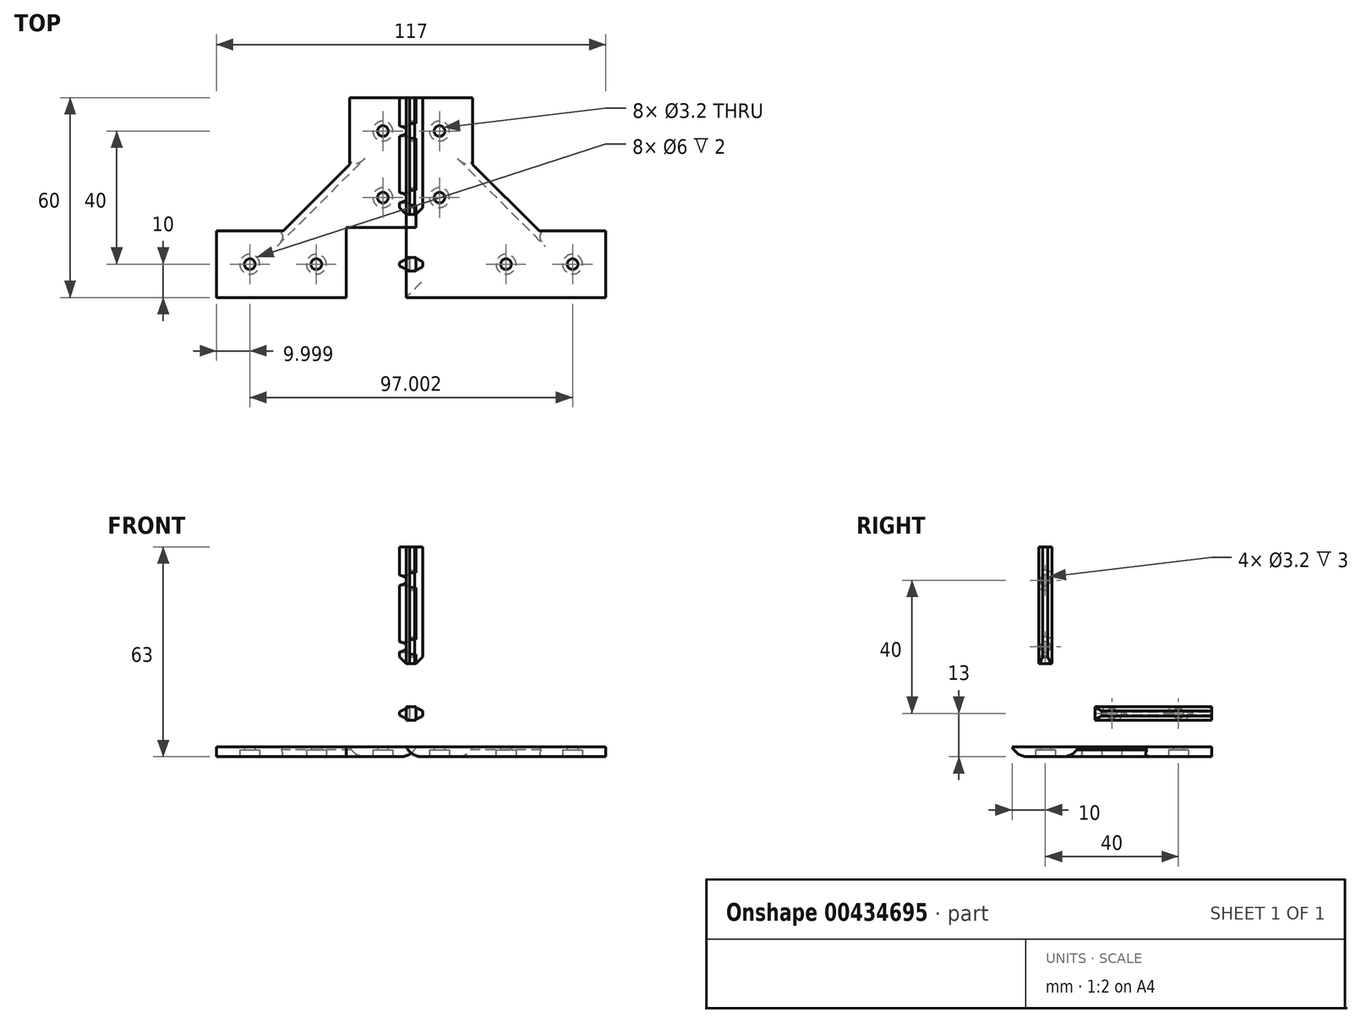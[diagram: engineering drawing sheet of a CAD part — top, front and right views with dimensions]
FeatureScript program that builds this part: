
annotation { "Feature Type Name" : "Feature", "Feature Type Description" : "" }
export const myFeature = defineFeature(function(context is Context, id is Id, definition is map)
    precondition{}
    {
        {
            var Q0;
            Q0=qCreatedBy(makeId("Right.planeOp"),FACE);
            var sketch = newSketch(context, id + "F0", { "sketchPlane" : qUnion([Q0])});
            skLineSegment(sketch, "E0", {"start": v(0, 0) * mm, "end": v(0, 50) * mm, "construction": true});
            skLineSegment(sketch, "E1", {"start": v(0, 0) * mm, "end": v(50, 0) * mm, "construction": true});
            skLineSegment(sketch, "E2", {"start": v(50, 10) * mm, "end": v(50, -10) * mm, "construction": true});
            skLineSegment(sketch, "E3", {"start": v(-10, 50) * mm, "end": v(10, 50) * mm, "construction": true});
            skLineSegment(sketch, "E4", {"start": v(-10, 50) * mm, "end": v(-10, -10) * mm});
            skLineSegment(sketch, "E5", {"start": v(50, -10) * mm, "end": v(-10, -10) * mm});
            skLineSegment(sketch, "E6.MirrorCS", {"start": v(10, 50) * mm, "end": v(10, 10) * mm, "construction": true});
            skLineSegment(sketch, "E7.MirrorCS", {"start": v(50, 10) * mm, "end": v(10, 10) * mm, "construction": true});
            skLineSegment(sketch, "E8", {"start": v(-10, 50) * mm, "end": v(10, 50) * mm});
            skLineSegment(sketch, "E9", {"start": v(50, 10) * mm, "end": v(50, -10) * mm});
            skLineSegment(sketch, "E10", {"start": v(50, 10) * mm, "end": v(10, 50) * mm, "construction": true});
            skLineSegment(sketch, "E11", {"start": v(10, 10) * mm, "end": v(10, -10) * mm, "construction": true});
            skLineSegment(sketch, "E12", {"start": v(10, 10) * mm, "end": v(-10, 10) * mm, "construction": true});
            skCircle(sketch, "E13", {"center": v(0, 40) * mm, "radius": 2 * mm, "construction": true});
            skCircle(sketch, "E14", {"center": v(0, 20) * mm, "radius": 2 * mm, "construction": true});
            skCircle(sketch, "E15", {"center": v(20, 0) * mm, "radius": 2 * mm, "construction": true});
            skCircle(sketch, "E16", {"center": v(40, 0) * mm, "radius": 2 * mm, "construction": true});
            skPoint(sketch, "E17", {"position": v(-2, 40) * mm});
            skPoint(sketch, "E18", {"position": v(2, 40) * mm});
            skPoint(sketch, "E19", {"position": v(-2, 20) * mm});
            skPoint(sketch, "E20", {"position": v(2, 20) * mm});
            skLineSegment(sketch, "E21", {"start": v(-2, 50) * mm, "end": v(-2, 15) * mm});
            skLineSegment(sketch, "E22", {"start": v(-2, 15) * mm, "end": v(2, 15) * mm});
            skLineSegment(sketch, "E23", {"start": v(2, 15) * mm, "end": v(2, 50) * mm});
            skPoint(sketch, "E24", {"position": v(20, -2) * mm});
            skPoint(sketch, "E25", {"position": v(20, 2) * mm});
            skPoint(sketch, "E26", {"position": v(40, 2) * mm});
            skPoint(sketch, "E27", {"position": v(40, -2) * mm});
            skLineSegment(sketch, "E28", {"start": v(15, 2) * mm, "end": v(15, -2) * mm});
            skLineSegment(sketch, "E29", {"start": v(50, 2) * mm, "end": v(15, 2) * mm});
            skLineSegment(sketch, "E30", {"start": v(50, -2) * mm, "end": v(15, -2) * mm});
            skLineSegment(sketch, "E31", {"start": v(10, 30) * mm, "end": v(30, 10) * mm});
            skLineSegment(sketch, "E32", {"start": v(30, 10) * mm, "end": v(50, 10) * mm});
            skLineSegment(sketch, "E33", {"start": v(10, 30) * mm, "end": v(10, 50) * mm});
            skLineSegment(sketch, "E34", {"start": v(11, 10) * mm, "end": v(11, -10) * mm});
            skLineSegment(sketch, "E35", {"start": v(10, 11) * mm, "end": v(-10, 11) * mm});
            skLineSegment(sketch, "E36", {"start": v(11, 10) * mm, "end": v(10, 10) * mm, "construction": true});
            skLineSegment(sketch, "E37", {"start": v(10, 11) * mm, "end": v(10, 10) * mm, "construction": true});
            skLineSegment(sketch, "E38", {"start": v(11, 10) * mm, "end": v(11, 11) * mm});
            skLineSegment(sketch, "E39", {"start": v(11, 11) * mm, "end": v(10, 11) * mm});
            skSolve(sketch);
        }
        {
            var Q0;
            {var subQ7=sQuery(id+"F0.wireOp",EDGE,"E4");Q0=makeQuery(id+"F0.imprint","IMPRINT",FACE,{"disambiguationData":[TD([[makeQuery(id+"F0.imprint","IMPRINT",EDGE,{"derivedFrom":subQ7}),1.0]])]});}
            var Q1;
            {var subQ0=sQuery(id+"F0.wireOp",EDGE,"E21");Q1=makeQuery(id+"F0.imprint","IMPRINT",FACE,{"disambiguationData":[TD([[makeQuery(id+"F0.imprint","IMPRINT",EDGE,{"derivedFrom":subQ0}),1.0]])]});}
            var Q2;
            Q2=makeQuery(id+"F0.imprint","IMPRINT",FACE,{"disambiguationData":[TD([[makeQuery(id+"F0.imprint","IMPRINT",EDGE,{"derivedFrom":sQuery(id+"F0.wireOp",EDGE,"E28")}),1.0]])]});
            var Q3;
            {var subQ1=sQuery(id+"F0.wireOp",EDGE,"E21");Q3=makeQuery(id+"F0.imprint","IMPRINT",FACE,{"disambiguationData":[TD([[makeQuery(id+"F0.imprint","IMPRINT",EDGE,{"derivedFrom":subQ1}),-1.0]])]});}
            extrude(context, id + "F1", {"entities" : qUnion([Q0, Q1, Q2, Q3]), "depth" : 3 * mm});
        }
        {
            var Q0;
            Q0=makeQuery(id+"F1.opExtrude","CAP_FACE",FACE,{"disambiguationData":[OSD([sQuery(id+"F0.wireOp",EDGE,"E4"),sQuery(id+"F0.wireOp",EDGE,"E5"),sQuery(id+"F0.wireOp",EDGE,"E8"),sQuery(id+"F0.wireOp",EDGE,"E9"),sQuery(id+"F0.wireOp",EDGE,"E10")])],"isStart":false});
            var sketch = newSketch(context, id + "F2", { "sketchPlane" : qUnion([Q0])});
            skPoint(sketch, "E40.0", {"position": v(0, 40) * mm});
            skPoint(sketch, "E40.1", {"position": v(0, 20) * mm});
            skPoint(sketch, "E40.2", {"position": v(20, 0) * mm});
            skPoint(sketch, "E40.3", {"position": v(40, 0) * mm});
            skSolve(sketch);
        }
        {
            var Q0;
            Q0=makeQuery(id+"F1.opExtrude","CAP_FACE",FACE,{"disambiguationData":[OSD([sQuery(id+"F0.wireOp",EDGE,"E4"),sQuery(id+"F0.wireOp",EDGE,"E5"),sQuery(id+"F0.wireOp",EDGE,"E8"),sQuery(id+"F0.wireOp",EDGE,"E9"),sQuery(id+"F0.wireOp",EDGE,"E10")])],"isStart":false});
            var sketch = newSketch(context, id + "F3", { "sketchPlane" : qUnion([Q0])});
            skLineSegment(sketch, "E41.0", {"start": v(50, 2) * mm, "end": v(15, 2) * mm});
            skLineSegment(sketch, "E41.1", {"start": v(50, -2) * mm, "end": v(15, -2) * mm});
            skLineSegment(sketch, "E41.2", {"start": v(15, 2) * mm, "end": v(15, -2) * mm});
            skLineSegment(sketch, "E41.3", {"start": v(50, 10) * mm, "end": v(50, -10) * mm});
            skLineSegment(sketch, "E41.4", {"start": v(-2, 15) * mm, "end": v(2, 15) * mm});
            skLineSegment(sketch, "E41.5", {"start": v(-2, 50) * mm, "end": v(-2, 15) * mm});
            skLineSegment(sketch, "E41.6", {"start": v(2, 15) * mm, "end": v(2, 50) * mm});
            skLineSegment(sketch, "E41.7", {"start": v(-10, 50) * mm, "end": v(10, 50) * mm});
            skSolve(sketch);
        }
        {
            var Q0;
            Q0=qSketchRegion(id+"F3",true);
            extrude(context, id + "F4", {"entities" : qUnion([Q0]), "oppositeDirection" : true, "depth" : 5 * mm});
        }
        {
            var Q0;
            Q0=makeQuery(id+"F4.opExtrude","CAP_EDGE",EDGE,{"disambiguationData":[OSD([sQuery(id+"F3.wireOp",EDGE,"E41.0")])],"isStart":false});
            var Q1;
            Q1=makeQuery(id+"F4.opExtrude","CAP_EDGE",EDGE,{"disambiguationData":[OSD([sQuery(id+"F3.wireOp",EDGE,"E41.1")])],"isStart":false});
            var Q2;
            Q2=makeQuery(id+"F4.opExtrude","CAP_EDGE",EDGE,{"disambiguationData":[OSD([sQuery(id+"F3.wireOp",EDGE,"E41.6")])],"isStart":false});
            var Q3;
            Q3=makeQuery(id+"F4.opExtrude","CAP_EDGE",EDGE,{"disambiguationData":[OSD([sQuery(id+"F3.wireOp",EDGE,"E41.5")])],"isStart":false});
            chamfer(context, id + "F5", {"entities" : qUnion([Q0, Q1, Q2, Q3]), "chamferType" : ChamferType.TWO_OFFSETS, "width1" : 3 * mm, "oppositeDirection" : false, "width2" : 1.5 * mm, "tangentPropagation" : true});
        }
        {
            var Q0;
            Q0=sQuery(id+"F2.wireOp",VERTEX,"E40.0");
            var Q1;
            Q1=sQuery(id+"F2.wireOp",VERTEX,"E40.1");
            var Q2;
            Q2=sQuery(id+"F2.wireOp",VERTEX,"E40.2");
            var Q3;
            Q3=sQuery(id+"F2.wireOp",VERTEX,"E40.3");
            var Q4;
            Q4=makeQuery(id+"F1.opExtrude","SWEPT_BODY",BODY,{"disambiguationData":[OSD([sQuery(id+"F0.wireOp",EDGE,"E4"),sQuery(id+"F0.wireOp",EDGE,"E5"),sQuery(id+"F0.wireOp",EDGE,"E8"),sQuery(id+"F0.wireOp",EDGE,"E9"),sQuery(id+"F0.wireOp",EDGE,"E10")])]});
            var Q5;
            Q5=makeQuery(id+"F4.opExtrude","SWEPT_BODY",BODY,{"disambiguationData":[OSD([sQuery(id+"F3.wireOp",EDGE,"E41.0"),sQuery(id+"F3.wireOp",EDGE,"E41.1"),sQuery(id+"F3.wireOp",EDGE,"E41.2"),sQuery(id+"F3.wireOp",EDGE,"E41.3")])]});
            var Q6;
            Q6=makeQuery(id+"F4.opExtrude","SWEPT_BODY",BODY,{"disambiguationData":[OSD([sQuery(id+"F3.wireOp",EDGE,"E41.4"),sQuery(id+"F3.wireOp",EDGE,"E41.5"),sQuery(id+"F3.wireOp",EDGE,"E41.6"),sQuery(id+"F3.wireOp",EDGE,"E41.7")])]});
            hole(context, id + "F6", {"style" : HoleStyle.C_BORE, "endStyle" : HoleEndStyle.THROUGH, "holeDiameter" : 3.2 * mm, "cBoreDiameter" : 6 * mm, "cBoreDepth" : 2 * mm, "isTappedThrough" : true, "tappedDepth" : 12 * mm, "tapClearance" : 3, "startFromSketch" : true, "locations" : qUnion([Q0, Q1, Q2, Q3]), "scope" : qUnion([Q4, Q5, Q6])});
        }
        {
            var Q0;
            Q0=makeQuery(id+"F1.opExtrude","CAP_EDGE",EDGE,{"disambiguationData":[OSD([sQuery(id+"F0.wireOp",EDGE,"E4")])],"isStart":false});
            var Q1;
            Q1=makeQuery(id+"F1.opExtrude","CAP_EDGE",EDGE,{"disambiguationData":[OSD([sQuery(id+"F0.wireOp",EDGE,"E5")])],"isStart":false});
            var Q2;
            Q2=makeQuery(id+"F1.opExtrude","CAP_EDGE",EDGE,{"disambiguationData":[OSD([sQuery(id+"F0.wireOp",EDGE,"E33")])],"isStart":false});
            var Q3;
            Q3=makeQuery(id+"F1.opExtrude","CAP_EDGE",EDGE,{"disambiguationData":[OSD([sQuery(id+"F0.wireOp",EDGE,"E32")])],"isStart":false});
            fillet(context, id + "F7", {"entities" : qUnion([Q0, Q1, Q2, Q3]), "radius" : 5 * mm, "tangentPropagation" : true, "allowEdgeOverflow" : false});
        }
        {
            var Q0;
            Q0=makeQuery(id+"F1.opExtrude","CAP_EDGE",EDGE,{"disambiguationData":[OSD([sQuery(id+"F0.wireOp",EDGE,"E31")])],"isStart":false});
            chamfer(context, id + "F8", {"entities" : qUnion([Q0]), "width" : 2 * mm, "tangentPropagation" : true});
        }
        {
            var Q0;
            Q0=makeQuery(id+"F4.opExtrude","CAP_EDGE",EDGE,{"disambiguationData":[OSD([sQuery(id+"F3.wireOp",EDGE,"E41.2")])],"isStart":false});
            var Q1;
            Q1=makeQuery(id+"F4.opExtrude","CAP_EDGE",EDGE,{"disambiguationData":[OSD([sQuery(id+"F3.wireOp",EDGE,"E41.4")])],"isStart":false});
            chamfer(context, id + "F9", {"entities" : qUnion([Q0, Q1]), "width" : 2 * mm, "tangentPropagation" : true});
        }
        {
            var Q0;
            Q0=makeQuery(id+"F1.opExtrude","SWEPT_BODY",BODY,{"disambiguationData":[OSD([sQuery(id+"F0.wireOp",EDGE,"E4"),sQuery(id+"F0.wireOp",EDGE,"E5"),sQuery(id+"F0.wireOp",EDGE,"E8"),sQuery(id+"F0.wireOp",EDGE,"E9"),sQuery(id+"F0.wireOp",EDGE,"E31"),sQuery(id+"F0.wireOp",EDGE,"E32"),sQuery(id+"F0.wireOp",EDGE,"E33")])]});
            var Q1;
            Q1=sQuery(id+"F0.wireOp",EDGE,"E5");
            transform(context, id + "F10", {"entities" : qUnion([Q0]), "transformType" : TransformType.ROTATION, "transformAxis" : qUnion([Q1]), "angle" : 270 * degree, "makeCopy" : false});
        }
        {
            var Q0;
            {var subQ0=sQuery(id+"F0.wireOp",EDGE,"E21");Q0=makeQuery(id+"F0.imprint","IMPRINT",FACE,{"disambiguationData":[TD([[makeQuery(id+"F0.imprint","IMPRINT",EDGE,{"derivedFrom":subQ0}),1.0]])]});}
            var Q1;
            Q1=makeQuery(id+"F0.imprint","IMPRINT",FACE,{"disambiguationData":[TD([[makeQuery(id+"F0.imprint","IMPRINT",EDGE,{"derivedFrom":sQuery(id+"F0.wireOp",EDGE,"E28")}),1.0]])]});
            var Q2;
            {var subQ1=sQuery(id+"F0.wireOp",EDGE,"E21");Q2=makeQuery(id+"F0.imprint","IMPRINT",FACE,{"disambiguationData":[TD([[makeQuery(id+"F0.imprint","IMPRINT",EDGE,{"derivedFrom":subQ1}),-1.0]])]});}
            extrude(context, id + "F11", {"entities" : qUnion([Q0, Q1, Q2]), "depth" : 3 * mm});
        }
        {
            var Q0;
            Q0=makeQuery(id+"F0.imprint","IMPRINT",FACE,{"disambiguationData":[TD([[makeQuery(id+"F0.imprint","IMPRINT",EDGE,{"derivedFrom":sQuery(id+"F0.wireOp",EDGE,"E28")}),1.0]])]});
            var Q1;
            {var subQ0=sQuery(id+"F0.wireOp",EDGE,"E21");Q1=makeQuery(id+"F0.imprint","IMPRINT",FACE,{"disambiguationData":[TD([[makeQuery(id+"F0.imprint","IMPRINT",EDGE,{"derivedFrom":subQ0}),1.0]])]});}
            extrude(context, id + "F12", {"entities" : qUnion([Q0, Q1]), "depth" : 5 * mm});
        }
        {
            var Q0;
            Q0=makeQuery(id+"F12.opExtrude","CAP_EDGE",EDGE,{"disambiguationData":[OSD([sQuery(id+"F0.wireOp",EDGE,"E29")])],"isStart":false});
            var Q1;
            Q1=makeQuery(id+"F12.opExtrude","CAP_EDGE",EDGE,{"disambiguationData":[OSD([sQuery(id+"F0.wireOp",EDGE,"E30")])],"isStart":false});
            var Q2;
            Q2=makeQuery(id+"F12.opExtrude","CAP_EDGE",EDGE,{"disambiguationData":[OSD([sQuery(id+"F0.wireOp",EDGE,"E23")])],"isStart":false});
            var Q3;
            Q3=makeQuery(id+"F12.opExtrude","CAP_EDGE",EDGE,{"disambiguationData":[OSD([sQuery(id+"F0.wireOp",EDGE,"E21")])],"isStart":false});
            chamfer(context, id + "F13", {"entities" : qUnion([Q0, Q1, Q2, Q3]), "chamferType" : ChamferType.TWO_OFFSETS, "width1" : 1.25 * mm, "oppositeDirection" : false, "width2" : 2.5 * mm, "tangentPropagation" : true});
        }
        {
            var Q0;
            {var subQ1=sQuery(id+"F0.wireOp",EDGE,"E21");Q0=makeQuery(id+"F0.imprint","IMPRINT",FACE,{"disambiguationData":[TD([[makeQuery(id+"F0.imprint","IMPRINT",EDGE,{"derivedFrom":subQ1}),-1.0]])]});}
            var sketch = newSketch(context, id + "F14", { "sketchPlane" : qUnion([Q0])});
            skPoint(sketch, "E42.0", {"position": v(20, 0) * mm});
            skPoint(sketch, "E42.1", {"position": v(40, 0) * mm});
            skPoint(sketch, "E42.2", {"position": v(0, 20) * mm});
            skPoint(sketch, "E42.3", {"position": v(0, 40) * mm});
            skSolve(sketch);
        }
        {
            var Q0;
            Q0=sQuery(id+"F14.wireOp",VERTEX,"E42.3");
            var Q1;
            Q1=sQuery(id+"F14.wireOp",VERTEX,"E42.2");
            var Q2;
            Q2=sQuery(id+"F14.wireOp",VERTEX,"E42.0");
            var Q3;
            Q3=sQuery(id+"F14.wireOp",VERTEX,"E42.1");
            var Q4;
            Q4=makeQuery(id+"F11.opExtrude","SWEPT_BODY",BODY,{"disambiguationData":[OSD([sQuery(id+"F0.wireOp",EDGE,"E4"),sQuery(id+"F0.wireOp",EDGE,"E5"),sQuery(id+"F0.wireOp",EDGE,"E8"),sQuery(id+"F0.wireOp",EDGE,"E9"),sQuery(id+"F0.wireOp",EDGE,"E31"),sQuery(id+"F0.wireOp",EDGE,"E32"),sQuery(id+"F0.wireOp",EDGE,"E33"),sQuery(id+"F0.wireOp",EDGE,"E34"),sQuery(id+"F0.wireOp",EDGE,"E35"),sQuery(id+"F0.wireOp",EDGE,"E38"),sQuery(id+"F0.wireOp",EDGE,"E39")])]});
            hole(context, id + "F15", {"style" : HoleStyle.C_BORE, "endStyle" : HoleEndStyle.THROUGH, "oppositeDirection" : true, "holeDiameter" : 3.2 * mm, "cBoreDiameter" : 6 * mm, "cBoreDepth" : 2 * mm, "isTappedThrough" : true, "tappedDepth" : 12 * mm, "tapClearance" : 3, "startFromSketch" : true, "locations" : qUnion([Q0, Q1, Q2, Q3]), "scope" : qUnion([Q4])});
        }
        {
            var Q0;
            Q0=makeQuery(id+"F11.opExtrude","CAP_EDGE",EDGE,{"disambiguationData":[OSD([sQuery(id+"F0.wireOp",EDGE,"E4")])],"isStart":true});
            var Q1;
            Q1=makeQuery(id+"F11.opExtrude","CAP_EDGE",EDGE,{"disambiguationData":[OSD([sQuery(id+"F0.wireOp",EDGE,"E5")])],"isStart":true});
            var Q2;
            Q2=makeQuery(id+"F11.opExtrude","CAP_EDGE",EDGE,{"disambiguationData":[OSD([sQuery(id+"F0.wireOp",EDGE,"E33")])],"isStart":true});
            var Q3;
            Q3=makeQuery(id+"F11.opExtrude","CAP_EDGE",EDGE,{"disambiguationData":[OSD([sQuery(id+"F0.wireOp",EDGE,"E32")])],"isStart":true});
            fillet(context, id + "F16", {"entities" : qUnion([Q0, Q1, Q2, Q3]), "radius" : 5 * mm, "tangentPropagation" : true, "allowEdgeOverflow" : false});
        }
        {
            var Q0;
            Q0=makeQuery(id+"F11.opExtrude","CAP_EDGE",EDGE,{"disambiguationData":[OSD([sQuery(id+"F0.wireOp",EDGE,"E31")])],"isStart":true});
            chamfer(context, id + "F17", {"entities" : qUnion([Q0]), "width" : 2 * mm, "tangentPropagation" : true});
        }
        {
            var Q0;
            Q0=makeQuery(id+"F12.opExtrude","CAP_EDGE",EDGE,{"disambiguationData":[OSD([sQuery(id+"F0.wireOp",EDGE,"E28")])],"isStart":false});
            var Q1;
            Q1=makeQuery(id+"F12.opExtrude","CAP_EDGE",EDGE,{"disambiguationData":[OSD([sQuery(id+"F0.wireOp",EDGE,"E22")])],"isStart":false});
            chamfer(context, id + "F18", {"entities" : qUnion([Q0, Q1]), "width" : 2 * mm, "tangentPropagation" : true});
        }
        {
            var Q0;
            Q0=makeQuery(id+"F11.opExtrude","SWEPT_BODY",BODY,{"disambiguationData":[OSD([sQuery(id+"F0.wireOp",EDGE,"E4"),sQuery(id+"F0.wireOp",EDGE,"E5"),sQuery(id+"F0.wireOp",EDGE,"E8"),sQuery(id+"F0.wireOp",EDGE,"E9"),sQuery(id+"F0.wireOp",EDGE,"E31"),sQuery(id+"F0.wireOp",EDGE,"E32"),sQuery(id+"F0.wireOp",EDGE,"E33"),sQuery(id+"F0.wireOp",EDGE,"E34"),sQuery(id+"F0.wireOp",EDGE,"E35"),sQuery(id+"F0.wireOp",EDGE,"E38"),sQuery(id+"F0.wireOp",EDGE,"E39")])]});
            var Q1;
            {var subQ0=sQuery(id+"F0.wireOp",EDGE,"E5");Q1=makeQuery(id+"F16.opFillet","BLEND_EDGE",EDGE,{"blendedFrom":[makeQuery(id+"F11.opExtrude","CAP_EDGE",EDGE,{"disambiguationData":[OSD([subQ0])],"isStart":true}),makeQuery(id+"F11.opExtrude","CAP_FACE",FACE,{"disambiguationData":[OSD([sQuery(id+"F0.wireOp",EDGE,"E4"),subQ0,sQuery(id+"F0.wireOp",EDGE,"E8"),sQuery(id+"F0.wireOp",EDGE,"E9"),sQuery(id+"F0.wireOp",EDGE,"E31"),sQuery(id+"F0.wireOp",EDGE,"E32"),sQuery(id+"F0.wireOp",EDGE,"E33"),sQuery(id+"F0.wireOp",EDGE,"E34"),sQuery(id+"F0.wireOp",EDGE,"E35"),sQuery(id+"F0.wireOp",EDGE,"E38"),sQuery(id+"F0.wireOp",EDGE,"E39")])],"isStart":false})],"blendedInto":[makeQuery(id+"F11.opExtrude","CAP_FACE",FACE,{"disambiguationData":[OSD([sQuery(id+"F0.wireOp",EDGE,"E4"),subQ0,sQuery(id+"F0.wireOp",EDGE,"E8"),sQuery(id+"F0.wireOp",EDGE,"E9"),sQuery(id+"F0.wireOp",EDGE,"E31"),sQuery(id+"F0.wireOp",EDGE,"E32"),sQuery(id+"F0.wireOp",EDGE,"E33"),sQuery(id+"F0.wireOp",EDGE,"E34"),sQuery(id+"F0.wireOp",EDGE,"E35"),sQuery(id+"F0.wireOp",EDGE,"E38"),sQuery(id+"F0.wireOp",EDGE,"E39")])],"isStart":false})]});}
            transform(context, id + "F19", {"entities" : qUnion([Q0]), "transformType" : TransformType.ROTATION, "transformAxis" : qUnion([Q1]), "angle" : 90 * degree, "makeCopy" : false});
        }
    });
